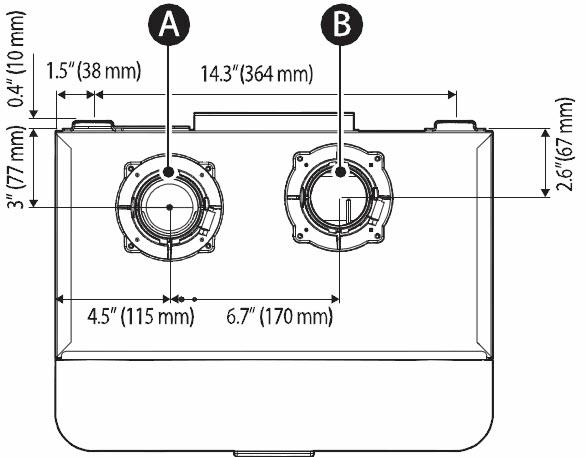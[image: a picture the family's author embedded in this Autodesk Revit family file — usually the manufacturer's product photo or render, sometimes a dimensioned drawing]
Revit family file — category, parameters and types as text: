
# Revit family: Water_Heater-Racks-Navien-NPE-9_Unit_Back_to_Back&Front---
name_source: partatom
category: Mechanical Equipment
revit_build: Autodesk Revit 2016 (Build: 20150220_1215(x64)
units: mm (PartAtom-declared; Revit-internal decimal feet)

## family parameters
Cut with Voids When Loaded = No
Host = Face
OmniClass Number = 23.65.35.11
OmniClass Title = Supply Water Heaters
Part Type = Normal
Room Calculation Point = No
Round Connector Dimension = Use Diameter
Shared = No

## types (4) — shared parameters
2" Exhaust/Intake = Yes
3" Exhaust/Intake = No
Apparent Load = 0 VA
Assembly Code = D3010500
Certifications = Energy Star | AHRI | CSA | CSA | NFS
Cold Water Inlet = 1"
Configuration = NPE_B9_4B2B_3F
Default Elevation = 48 "
Depth = 23.8 "
Description = 9 Unit Back to Back & Front
Exhaust = 2"
Finish = Metal - Navien - White
Flow Rate = 1 GPM
Flow Rate Note = 35°F (19°C) temp rise: 11.2 GPM (42 L/m) | 45°F (25°C) temp rise: 8.7 GPM (33 L/m) | 67°F (36°C) temp rise: NPE-240A: 5.6 GPM(21 L/m), NPE-240S: 5.7 GPM(22 L/m)
Frequency = 60 Hz
Gas Inlet = 1"
Heating Capacity = 120000.0 Btu/h
Heating Capacity Note = 19,900–199,900 (BTU/H)
Height = 65.5 "
Hot Water Outlet = 1"
Ignition = Electronic ignition
Installation Type = Indoor
Intake = 2"
Keynote = 22 33 00.A1
Manifold(s) = (1) 30019041A + (1) 30019039A + (1) 30019042A
Manufacturer = Navien, Inc.
Manufacturer Fax Number = (949) 420-0430
Natural Gas Manifold Pressure = -0.05" WC to -0.58" WC
Natural Gas Supply Pressure = 3.5"–10.5" WC
Number of Poles = 1
Phase = 1
Power Factor = 1
Product Documentation Link = https://www.navieninc.com
Product Name = NPE Series Tankless Water Heaters w/ Racks
Product Page URL = https://www.navieninc.com
Propane Gas Manifold Pressure = -0.10" WC to -0.78" WC
Propane Gas Supply Pressure = 8"–13" WC
Rack(s) = (2) GFFM-KDIZUS-003 + (4) GFFM-KDIZUS-004
Required Cascade Operation Accessory = (9) 30014367A (Common Vent Damper & Cascade Communication Cable) or (8) GXXX000546 (Individual Vent Cascade Communication Cable)
URL = https://www.navieninc.com
Venting = Exhaust: 2" PVC, CPVC, PP, SS / 2" special gas vent type BH (Class II, A/B/C) | Intake: 2" PVC, CPVC, PP, SS / 2" special gas vent type BH (Class II, A/B/C) | Vent clearances: 0" to combustibles
Venting Type = Forced draft direct vent
Version = 2016 - v1.0.a
Voltage = 120 V
Water Pressure = 15–150 PSI
Wi-Fi Ready = NaviLink Wi-Fi Control: PBCM-AS-001
Width = 142.3 "

## per-type parameters (varying)
| type | Constraints | Model | Natural Gas | Propane Gas | Recirculation Inlet | Recirculation Inlet Visibility | Tankless Water Heaters | Weight |
| Natural Gas - Recirculating System - NPE-240A(Advanced)-NG | 6 | (9) NPE-240A-NG | Yes | No | 0" | Yes | (9) NPE-240A-NG | 82.00 lbf |
| Natural Gas - NPE-240S(Standard)-NG | 7 | (9) NPE-240S-NG | Yes | No | 1" | No | (9) NPE-240S-NG | 75.00 lbf |
| Propane Gas - Recirculating System - NPE-240A(Advanced)-LPG | 6 | (9) NPE-240A-LPG | No | Yes | 0" | Yes | (9) NPE-240A-LPG | 82.00 lbf |
| Propane Gas - NPE-240S(Standard)-LPG | 7 | (9) NPE-240S-LPG | No | Yes | 1" | No | (9) NPE-240S-LPG | 75.00 lbf |

## geometry (parser evidence)
native form markers: Sweep x19
no freeform markers — native parametric forms only
